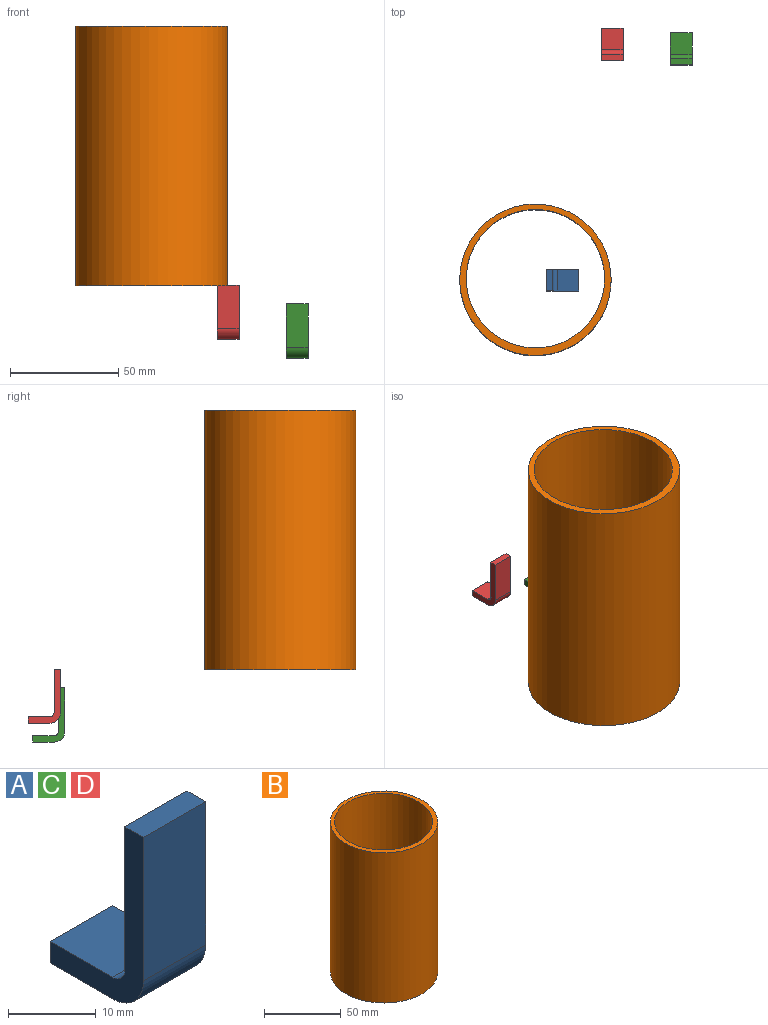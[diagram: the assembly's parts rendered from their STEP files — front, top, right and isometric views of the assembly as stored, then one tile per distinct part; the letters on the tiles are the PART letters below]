
ASSEMBLY  parts=4 mates=1
PART A: 10 faces, bbox 10x15x25 mm
  f0: plane 10x3mm, normal (0,0,1), area 30mm2, adj f1,f7,f8,f9
  f1: plane 20x10mm, normal (0,-1,0), area 200mm2, adj f0,f2,f8,f9
  f2: cylinder r=5mm len=10mm, axis (-1,0,0), area 78.5mm2, adj f1,f3,f8,f9
  f3: plane 10x10mm, normal (0,0,-1), area 100mm2, adj f2,f4,f8,f9
  f4: plane 10x3mm, normal (0,1,0), area 30mm2, adj f3,f5,f8,f9
  f5: plane 10x10mm, normal (0,0,1), area 100mm2, adj f4,f6,f8,f9
  f6: cylinder r=2mm len=10mm, axis (-1,0,0), area 31.4mm2, adj f5,f7,f8,f9
  f7: plane 20x10mm, normal (0,1,0), area 200mm2, adj f0,f6,f8,f9
  f8: plane 25x15mm, normal (1,0,0), area 106.5mm2, adj f0,f1,f2,f3,f4,f5,f6,f7
  f9: plane 25x15mm, normal (-1,0,0), area 106.5mm2, adj f0,f1,f2,f3,f4,f5,f6,f7
PART B: 4 faces, bbox 70x70x120 mm
  f0: cylinder r=32mm len=120mm, axis (0,0,-1), area 24127.4mm2, adj f2,f3
  f1: cylinder r=35mm len=120mm, axis (0,0,-1), area 26389.4mm2, adj f2,f3
  f2: plane 70x70mm, normal (0,0,1), area 631.5mm2, adj f0,f1
  f3: plane 70x70mm, normal (0,0,-1), area 631.5mm2, adj f0,f1
PART C: same geometry as A
PART D: same geometry as A
PLACE A rot(axis=(0,0,-1),90deg) t=(5,0,0)mm
PLACE B at identity fixed
PLACE C t=(67.44,99.53,-33.5)mm
PLACE D t=(35.52,101.58,-24.84)mm
MATE planar A.f3 <-> B.f3  axis (0,0,-1) through (15,0,0)mm
